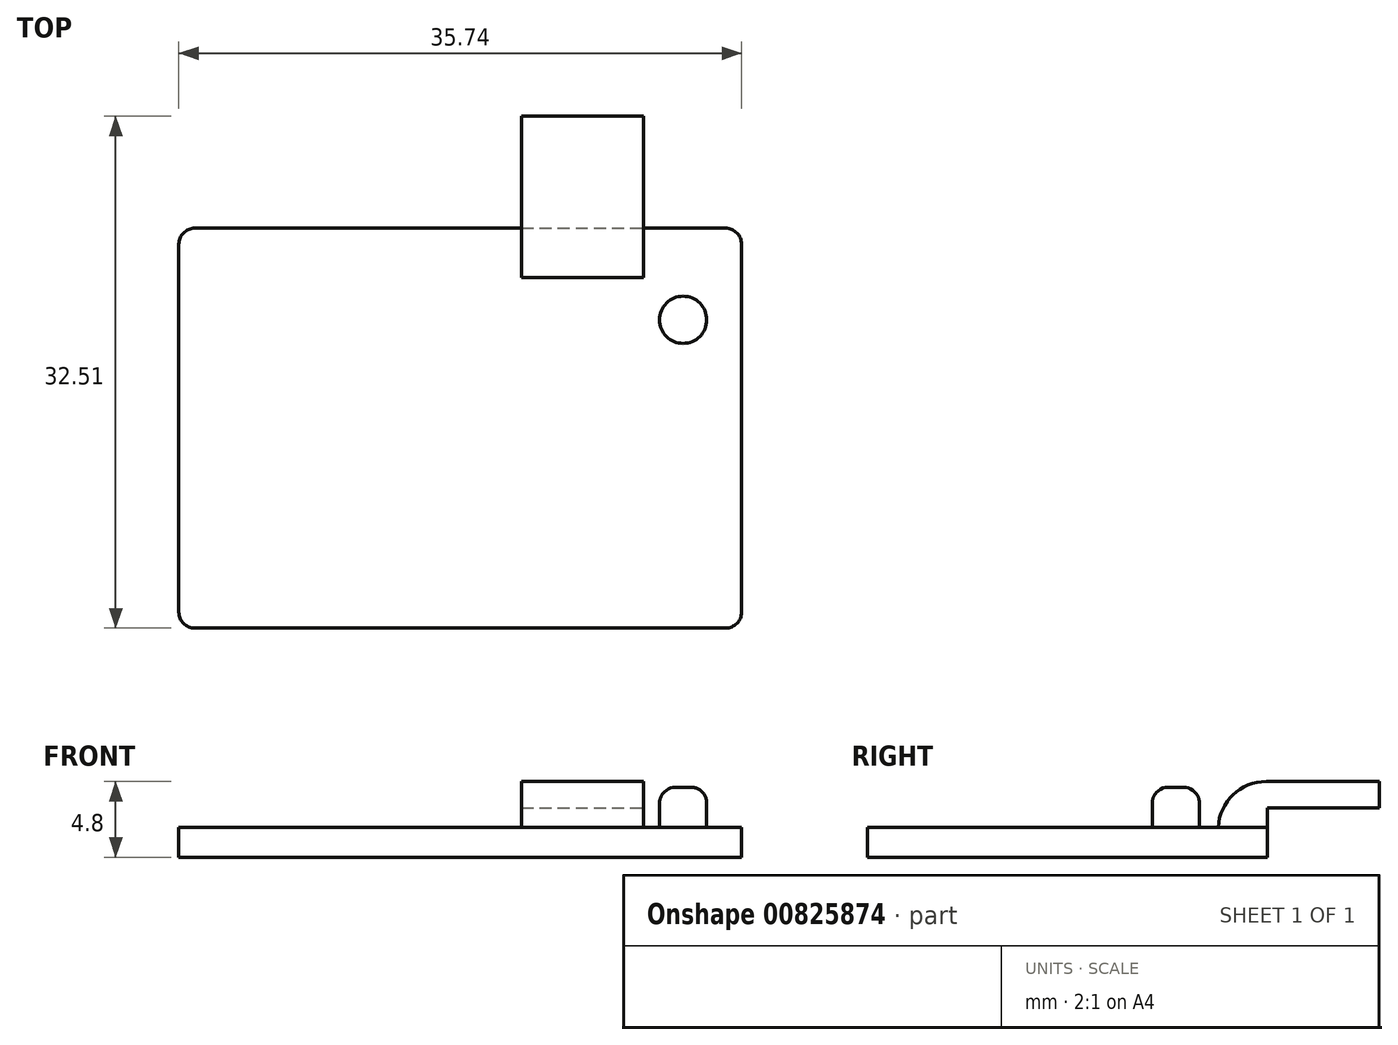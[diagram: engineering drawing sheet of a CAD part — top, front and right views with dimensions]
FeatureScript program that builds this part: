
annotation { "Feature Type Name" : "Feature", "Feature Type Description" : "" }
export const myFeature = defineFeature(function(context is Context, id is Id, definition is map)
    precondition{}
    {
        {
            var Q0;
            Q0=qCreatedBy(makeId("Top.planeOp"),FACE);
            var sketch = newSketch(context, id + "F0", { "sketchPlane" : qUnion([Q0])});
            skLineSegment(sketch, "E0.bottom", {"start": v(-17.87, 12.7) * mm, "end": v(17.87, 12.7) * mm});
            skLineSegment(sketch, "E0.top", {"start": v(-17.87, -12.7) * mm, "end": v(17.87, -12.7) * mm});
            skLineSegment(sketch, "E0.left", {"start": v(-17.87, 12.7) * mm, "end": v(-17.87, -12.7) * mm});
            skLineSegment(sketch, "E0.right", {"start": v(17.87, 12.7) * mm, "end": v(17.87, -12.7) * mm});
            skPoint(sketch, "E0.middle", {"position": v(0, 0) * mm});
            skSolve(sketch);
        }
        {
            var Q0;
            Q0=makeQuery(id+"F0.imprint","IMPRINT",FACE,{"disambiguationData":[TD([[makeQuery(id+"F0.imprint","IMPRINT",EDGE,{"derivedFrom":sQuery(id+"F0.wireOp",EDGE,"E0.bottom")}),-1.0]])]});
            extrude(context, id + "F1", {"entities" : qUnion([Q0]), "depth" : 1.9 * mm, "offsetDistance" : 25.4 * mm});
        }
        {
            var Q0;
            Q0=makeQuery(id+"F1.opExtrude","CAP_FACE",FACE,{"disambiguationData":[OSD([sQuery(id+"F0.wireOp",EDGE,"E0.bottom"),sQuery(id+"F0.wireOp",EDGE,"E0.top"),sQuery(id+"F0.wireOp",EDGE,"E0.left"),sQuery(id+"F0.wireOp",EDGE,"E0.right")])],"isStart":false});
            var sketch = newSketch(context, id + "F2", { "sketchPlane" : qUnion([Q0])});
            skCircle(sketch, "E1", {"center": v(14.16, 6.88) * mm, "radius": 1.5 * mm});
            skSolve(sketch);
        }
        {
            var Q0;
            Q0 = qSketchRegion(id + "F2", true);
            extrude(context, id + "F3", {"entities" : qUnion([Q0]), "operationType" : NewBodyOperationType.ADD, "depth" : 2.54 * mm, "offsetDistance" : 25.4 * mm});
        }
        {
            var Q0;
            Q0=makeQuery(id+"F3.opExtrude","CAP_EDGE",EDGE,{"disambiguationData":[OSD([sQuery(id+"F2.wireOp",EDGE,"E1")])],"isStart":false});
            fillet(context, id + "F4", {"entities" : qUnion([Q0]), "radius" : 1.02 * mm, "tangentPropagation" : true, "allowEdgeOverflow" : false});
        }
        {
            var Q0;
            Q0=makeQuery(id+"F1.opExtrude","CAP_FACE",FACE,{"disambiguationData":[OSD([sQuery(id+"F0.wireOp",EDGE,"E0.bottom"),sQuery(id+"F0.wireOp",EDGE,"E0.top"),sQuery(id+"F0.wireOp",EDGE,"E0.left"),sQuery(id+"F0.wireOp",EDGE,"E0.right")])],"isStart":false});
            var sketch = newSketch(context, id + "F5", { "sketchPlane" : qUnion([Q0])});
            skLineSegment(sketch, "E2.bottom", {"start": v(3.9, 9.58) * mm, "end": v(11.65, 9.58) * mm});
            skLineSegment(sketch, "E2.top", {"start": v(3.9, 19.81) * mm, "end": v(11.65, 19.81) * mm});
            skLineSegment(sketch, "E2.left", {"start": v(3.9, 9.58) * mm, "end": v(3.9, 19.81) * mm});
            skLineSegment(sketch, "E2.right", {"start": v(11.65, 9.58) * mm, "end": v(11.65, 19.81) * mm});
            skSolve(sketch);
        }
        {
            var Q0;
            Q0 = qSketchRegion(id + "F5", true);
            extrude(context, id + "F6", {"entities" : qUnion([Q0]), "operationType" : NewBodyOperationType.ADD, "depth" : 2.9 * mm, "offsetDistance" : 25.4 * mm});
        }
        {
            var Q0;
            Q0=makeQuery(id+"F6.opExtrude","SWEPT_FACE",FACE,{"disambiguationData":[OSD([sQuery(id+"F5.wireOp",EDGE,"E2.right")])]});
            var sketch = newSketch(context, id + "F7", { "sketchPlane" : qUnion([Q0])});
            skLineSegment(sketch, "E3.bottom", {"start": v(12.7, 1.9) * mm, "end": v(19.81, 1.9) * mm});
            skLineSegment(sketch, "E3.top", {"start": v(12.7, 3.12) * mm, "end": v(19.81, 3.12) * mm});
            skLineSegment(sketch, "E3.left", {"start": v(12.7, 1.9) * mm, "end": v(12.7, 3.12) * mm});
            skLineSegment(sketch, "E3.right", {"start": v(19.81, 1.9) * mm, "end": v(19.81, 3.12) * mm});
            skSolve(sketch);
        }
        {
            var Q0;
            Q0 = qSketchRegion(id + "F7", true);
            extrude(context, id + "F8", {"entities" : qUnion([Q0]), "operationType" : NewBodyOperationType.REMOVE, "endBound" : BoundingType.THROUGH_ALL, "oppositeDirection" : true, "depth" : 25.4 * mm, "offsetDistance" : 25.4 * mm});
        }
        {
            var Q0;
            Q0=makeQuery(id+"F6.opExtrude","CAP_EDGE",EDGE,{"disambiguationData":[OSD([sQuery(id+"F5.wireOp",EDGE,"E2.bottom")])],"isStart":false});
            fillet(context, id + "F9", {"entities" : qUnion([Q0]), "radius" : 3.05 * mm, "tangentPropagation" : true, "allowEdgeOverflow" : false});
        }
        {
            var Q0;
            Q0=makeQuery(id+"F1.opExtrude","SWEPT_EDGE",EDGE,{"disambiguationData":[OSD([sQuery(id+"F0.wireOp",EDGE,"E0.top"),sQuery(id+"F0.wireOp",EDGE,"E0.left")])]});
            var Q1;
            Q1=makeQuery(id+"F1.opExtrude","SWEPT_EDGE",EDGE,{"disambiguationData":[OSD([sQuery(id+"F0.wireOp",EDGE,"E0.top"),sQuery(id+"F0.wireOp",EDGE,"E0.right")])]});
            var Q2;
            Q2=makeQuery(id+"F1.opExtrude","SWEPT_EDGE",EDGE,{"disambiguationData":[OSD([sQuery(id+"F0.wireOp",EDGE,"E0.bottom"),sQuery(id+"F0.wireOp",EDGE,"E0.right")])]});
            var Q3;
            Q3=makeQuery(id+"F1.opExtrude","SWEPT_EDGE",EDGE,{"disambiguationData":[OSD([sQuery(id+"F0.wireOp",EDGE,"E0.bottom"),sQuery(id+"F0.wireOp",EDGE,"E0.left")])]});
            fillet(context, id + "F10", {"entities" : qUnion([Q0, Q1, Q2, Q3]), "radius" : 1.02 * mm, "tangentPropagation" : true, "allowEdgeOverflow" : false});
        }
    });
